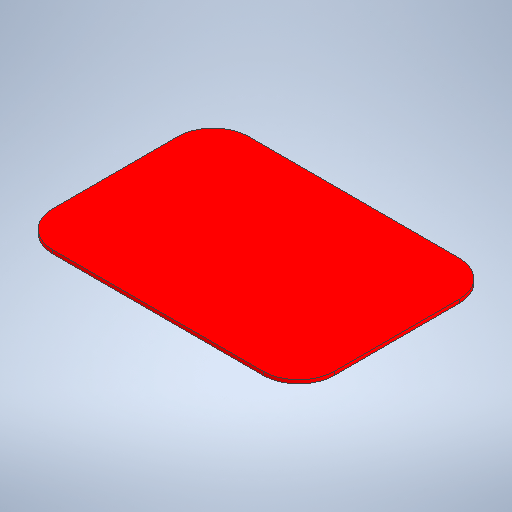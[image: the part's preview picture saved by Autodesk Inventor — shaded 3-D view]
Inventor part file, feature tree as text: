
AUTODESK INVENTOR PART (.ipt)
format: ipt  version: 2025.2 (Build 292293000, 293)  size: 236,032 bytes
history: native  units: mm
features: extrude x1, sketch x1
ambient origin geometry x8: Origin, YZ Plane, XZ Plane, XY Plane, X Axis, Y Axis, Z Axis, Center Point
bodies: Solid1 (feature_tree)
feature tree (2):
  extrude  "Extrusion1"  Depth=79.0mm
  sketch  "Sketch1"  dims[d0=55.0mm d1=79.0mm d2=1.0mm d3=0.0mm d4=10.0mm]
